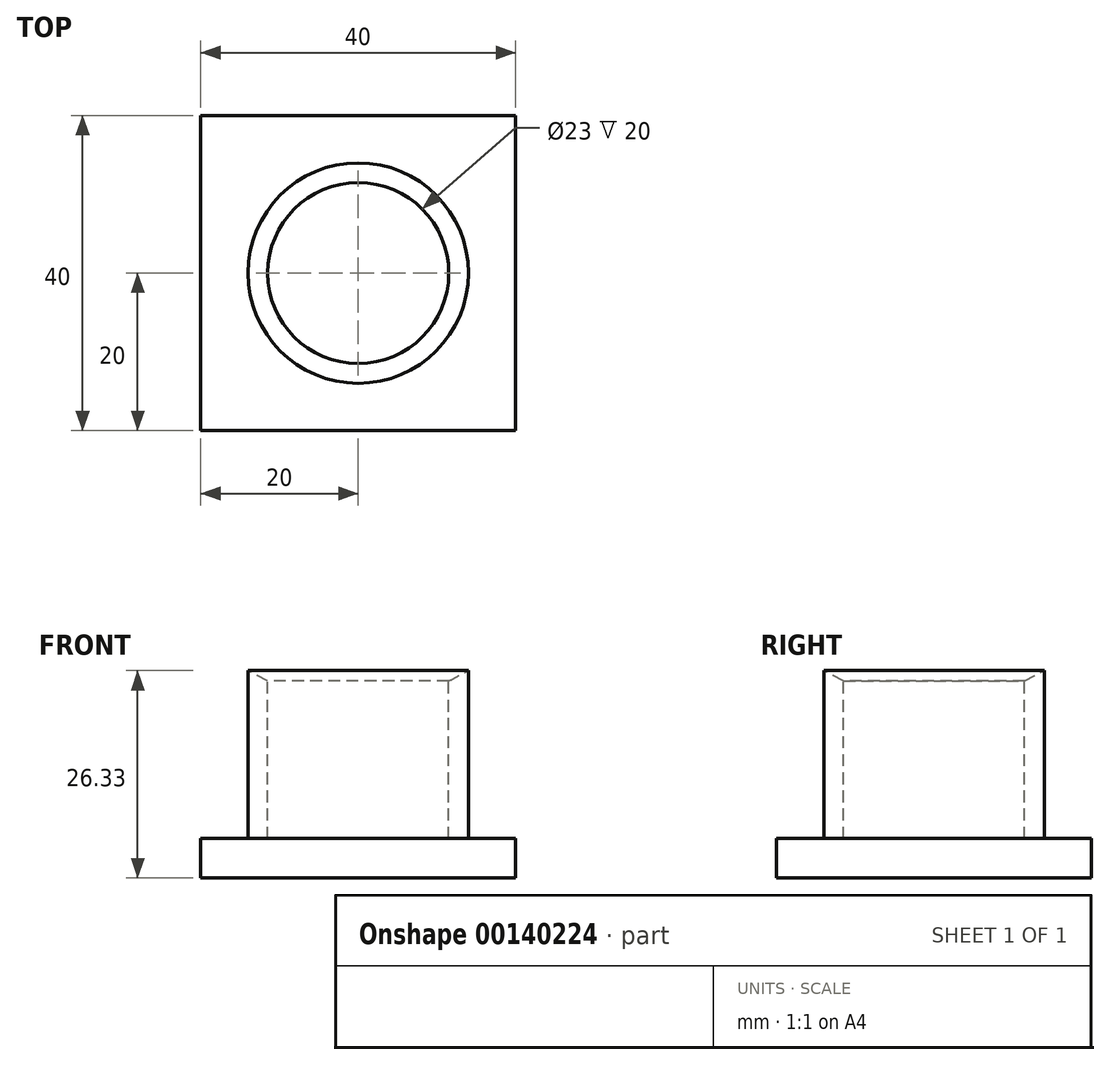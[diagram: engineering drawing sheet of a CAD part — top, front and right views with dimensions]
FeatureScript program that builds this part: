
annotation { "Feature Type Name" : "Feature", "Feature Type Description" : "" }
export const myFeature = defineFeature(function(context is Context, id is Id, definition is map)
    precondition{}
    {
        {
            var Q0;
            Q0=qCreatedBy(makeId("Top.planeOp"),FACE);
            var sketch = newSketch(context, id + "F0", { "sketchPlane" : qUnion([Q0])});
            skLineSegment(sketch, "E0", {"start": v(0, 65.15) * mm, "end": v(0, -74.15) * mm, "construction": true});
            skLineSegment(sketch, "E1", {"start": v(-73.04, 0) * mm, "end": v(85.28, 0) * mm, "construction": true});
            skLineSegment(sketch, "E2.bottom", {"start": v(20, 20) * mm, "end": v(-20, 20) * mm});
            skLineSegment(sketch, "E2.top", {"start": v(20, -20) * mm, "end": v(-20, -20) * mm});
            skLineSegment(sketch, "E2.left", {"start": v(20, 20) * mm, "end": v(20, -20) * mm});
            skLineSegment(sketch, "E2.right", {"start": v(-20, 20) * mm, "end": v(-20, -20) * mm});
            skPoint(sketch, "E2.middle", {"position": v(0, 0) * mm});
            skSolve(sketch);
        }
        {
            var Q0;
            Q0=qSketchRegion(id+"F0",true);
            extrude(context, id + "F1", {"entities" : qUnion([Q0]), "depth" : 5 * mm});
        }
        {
            var Q0;
            Q0=qCreatedBy(makeId("Front.planeOp"),FACE);
            var sketch = newSketch(context, id + "F2", { "sketchPlane" : qUnion([Q0])});
            skLineSegment(sketch, "E3", {"start": v(-33.59, 0) * mm, "end": v(32.44, 0) * mm, "construction": true});
            skLineSegment(sketch, "E4", {"start": v(0, 41.04) * mm, "end": v(0, -5.6) * mm, "construction": true});
            skLineSegment(sketch, "E5.right", {"start": v(-14, 5) * mm, "end": v(-14, 26.33) * mm});
            skLineSegment(sketch, "E6", {"start": v(-14, 26.33) * mm, "end": v(-11.5, 25) * mm});
            skLineSegment(sketch, "E7", {"start": v(-11.5, 25) * mm, "end": v(-11.5, 5) * mm});
            skLineSegment(sketch, "E8", {"start": v(-11.5, 5) * mm, "end": v(-14, 5) * mm});
            skLineSegment(sketch, "E9", {"start": v(-11.5, 25) * mm, "end": v(-14, 25) * mm, "construction": true});
            skSolve(sketch);
        }
        {
            var Q0;
            Q0 = qSketchRegion(id + "F2", true);
            var Q1;
            Q1=sQuery(id+"F2.wireOp",EDGE,"E4");
            revolve(context, id + "F3", {"operationType" : NewBodyOperationType.ADD, "entities" : qUnion([Q0]), "axis" : qUnion([Q1]), "revolveType" : RevolveType.FULL});
        }
    });
